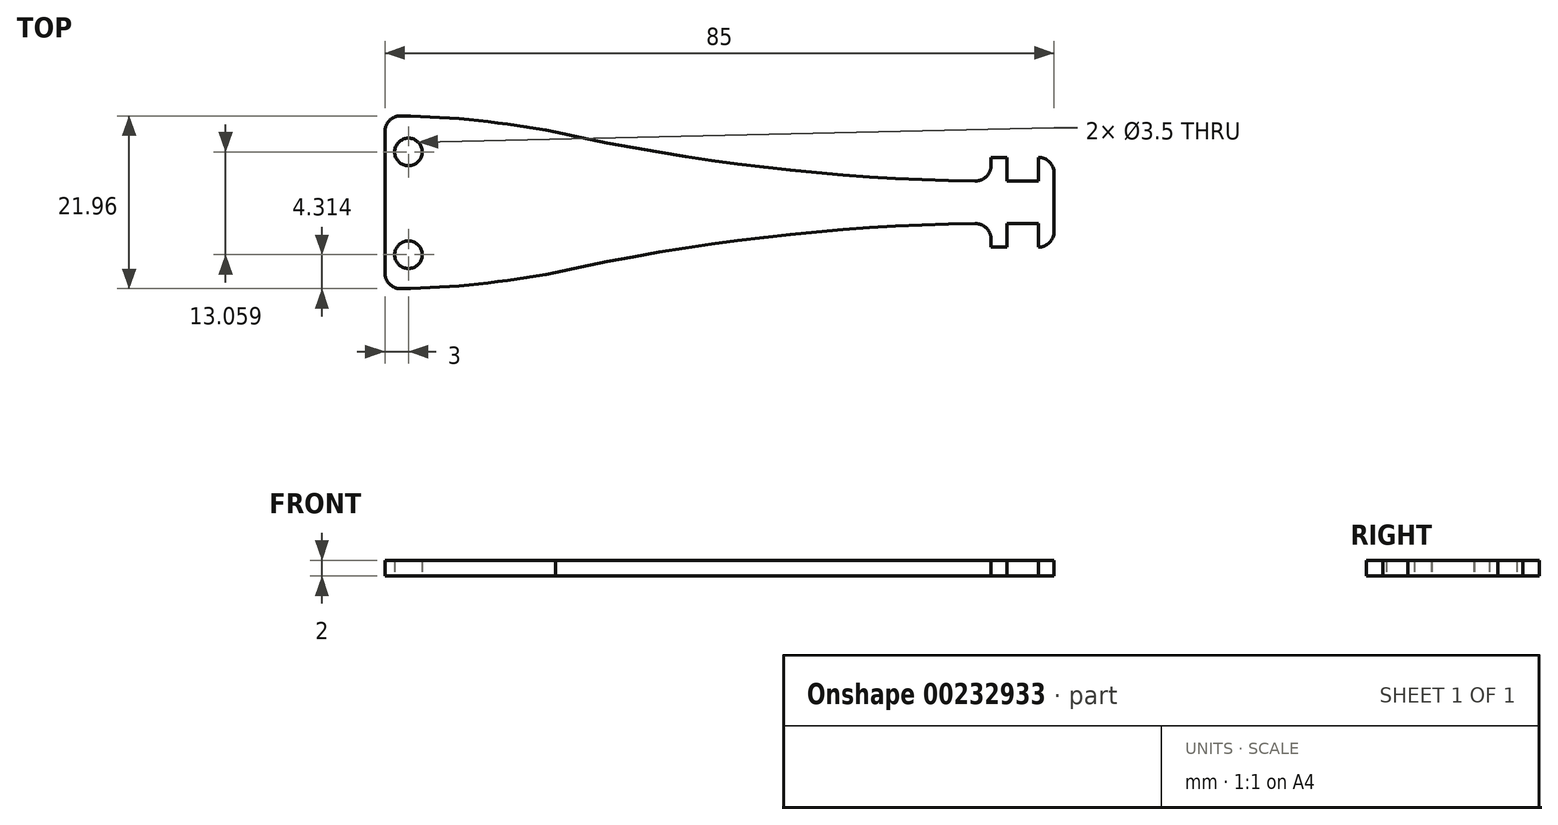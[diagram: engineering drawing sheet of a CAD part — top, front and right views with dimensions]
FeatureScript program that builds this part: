
annotation { "Feature Type Name" : "Feature", "Feature Type Description" : "" }
export const myFeature = defineFeature(function(context is Context, id is Id, definition is map)
    precondition{}
    {
        {
            var Q0;
            Q0=qCreatedBy(makeId("Top.planeOp"),FACE);
            var sketch = newSketch(context, id + "F0", { "sketchPlane" : qUnion([Q0])});
            skLineSegment(sketch, "E0.bottom", {"start": v(0, 0) * mm, "end": v(85, 0) * mm});
            skLineSegment(sketch, "E0.top", {"start": v(0, 22) * mm, "end": v(85, 22) * mm});
            skLineSegment(sketch, "E0.left", {"start": v(0, 0) * mm, "end": v(0, 22) * mm});
            skLineSegment(sketch, "E0.right", {"start": v(85, 0) * mm, "end": v(85, 22) * mm});
            skPoint(sketch, "E1", {"position": v(3, 11) * mm});
            skPoint(sketch, "E1.positionSnap0", {"position": v(0, 11) * mm});
            skCircle(sketch, "E2", {"center": v(3, 4.33) * mm, "radius": 1.75 * mm});
            skCircle(sketch, "E3", {"center": v(3, 17.4) * mm, "radius": 1.75 * mm});
            skArc(sketch, "E4", {"start": v(0, 0) * mm, "mid": v(10.88, 0.52) * mm, "end": v(21.66, 2.08) * mm});
            skArc(sketch, "E5", {"start": v(85, 8.26) * mm, "mid": v(53.14, 7.08) * mm, "end": v(21.66, 2.08) * mm});
            skLineSegment(sketch, "E6", {"start": v(85, 5.3) * mm, "end": v(83, 5.3) * mm});
            skLineSegment(sketch, "E7", {"start": v(83, 5.3) * mm, "end": v(83, 8.3) * mm});
            skLineSegment(sketch, "E8", {"start": v(79, 5.3) * mm, "end": v(79, 8.4) * mm});
            skLineSegment(sketch, "E9", {"start": v(79, 5.3) * mm, "end": v(77, 5.3) * mm});
            skLineSegment(sketch, "E10", {"start": v(77, 5.3) * mm, "end": v(77, 8.32) * mm});
            skLineSegment(sketch, "E11", {"start": v(3, 11) * mm, "end": v(13.42, 11) * mm, "construction": true});
            skArc(sketch, "E12.MirrorCS", {"start": v(85, 13.74) * mm, "mid": v(53.14, 14.92) * mm, "end": v(21.66, 19.92) * mm});
            skArc(sketch, "E13.MirrorCS", {"start": v(0, 22) * mm, "mid": v(10.88, 21.48) * mm, "end": v(21.66, 19.92) * mm});
            skLineSegment(sketch, "E14.MirrorCS", {"start": v(79, 16.7) * mm, "end": v(79, 13.6) * mm});
            skLineSegment(sketch, "E15.MirrorCS", {"start": v(79, 16.7) * mm, "end": v(77, 16.7) * mm});
            skLineSegment(sketch, "E16.MirrorCS", {"start": v(77, 16.7) * mm, "end": v(77, 13.68) * mm});
            skLineSegment(sketch, "E17.MirrorCS", {"start": v(83, 16.7) * mm, "end": v(83, 13.7) * mm});
            skLineSegment(sketch, "E18.MirrorCS", {"start": v(85, 16.7) * mm, "end": v(83, 16.7) * mm});
            skSolve(sketch);
        }
        {
            var Q0;
            Q0=makeQuery(id+"F0.imprint","IMPRINT",FACE,{"disambiguationData":[TD([[makeQuery(id+"F0.imprint","IMPRINT",EDGE,{"derivedFrom":sQuery(id+"F0.wireOp",EDGE,"E0.left")}),-1.0]])]});
            var Q1;
            {var subQ4=sQuery(id+"F0.wireOp",EDGE,"E9");Q1=makeQuery(id+"F0.imprint","IMPRINT",FACE,{"disambiguationData":[TD([[makeQuery(id+"F0.imprint","IMPRINT",EDGE,{"derivedFrom":subQ4}),-1.0]])]});}
            var Q2;
            {var subQ3=sQuery(id+"F0.wireOp",EDGE,"E6");Q2=makeQuery(id+"F0.imprint","IMPRINT",FACE,{"disambiguationData":[TD([[makeQuery(id+"F0.imprint","IMPRINT",EDGE,{"derivedFrom":subQ3}),-1.0]])]});}
            var Q3;
            {var subQ4=sQuery(id+"F0.wireOp",EDGE,"E15.MirrorCS");Q3=makeQuery(id+"F0.imprint","IMPRINT",FACE,{"disambiguationData":[TD([[makeQuery(id+"F0.imprint","IMPRINT",EDGE,{"derivedFrom":subQ4}),1.0]])]});}
            var Q4;
            {var subQ4=sQuery(id+"F0.wireOp",EDGE,"E17.MirrorCS");Q4=makeQuery(id+"F0.imprint","IMPRINT",FACE,{"disambiguationData":[TD([[makeQuery(id+"F0.imprint","IMPRINT",EDGE,{"derivedFrom":subQ4}),1.0]])]});}
            extrude(context, id + "F1", {"entities" : qUnion([Q0, Q1, Q2, Q3, Q4]), "depth" : 2 * mm});
        }
        {
            var Q0;
            Q0=makeQuery(id+"F1.opExtrude","SWEPT_EDGE",EDGE,{"disambiguationData":[OSD([sQuery(id+"F0.wireOp",EDGE,"E0.bottom"),sQuery(id+"F0.wireOp",EDGE,"E0.left"),sQuery(id+"F0.wireOp",EDGE,"E4")])]});
            var Q1;
            Q1=makeQuery(id+"F1.opExtrude","SWEPT_EDGE",EDGE,{"disambiguationData":[OSD([sQuery(id+"F0.wireOp",EDGE,"E0.top"),sQuery(id+"F0.wireOp",EDGE,"E0.left"),sQuery(id+"F0.wireOp",EDGE,"E13.MirrorCS")])]});
            var Q2;
            Q2=makeQuery(id+"F1.opExtrude","SWEPT_EDGE",EDGE,{"disambiguationData":[OSD([sQuery(id+"F0.wireOp",EDGE,"E0.right"),sQuery(id+"F0.wireOp",EDGE,"E6")])]});
            var Q3;
            Q3=makeQuery(id+"F1.opExtrude","SWEPT_EDGE",EDGE,{"disambiguationData":[OSD([sQuery(id+"F0.wireOp",EDGE,"E0.right"),sQuery(id+"F0.wireOp",EDGE,"E18.MirrorCS")])]});
            var Q4;
            Q4=makeQuery(id+"F1.opExtrude","SWEPT_EDGE",EDGE,{"disambiguationData":[OSD([sQuery(id+"F0.wireOp",EDGE,"E5"),sQuery(id+"F0.wireOp",EDGE,"E10")])]});
            var Q5;
            Q5=makeQuery(id+"F1.opExtrude","SWEPT_EDGE",EDGE,{"disambiguationData":[OSD([sQuery(id+"F0.wireOp",EDGE,"E12.MirrorCS"),sQuery(id+"F0.wireOp",EDGE,"E16.MirrorCS")])]});
            fillet(context, id + "F2", {"entities" : qUnion([Q0, Q1, Q2, Q3, Q4, Q5]), "radius" : 2 * mm, "tangentPropagation" : true, "allowEdgeOverflow" : false});
        }
    });
